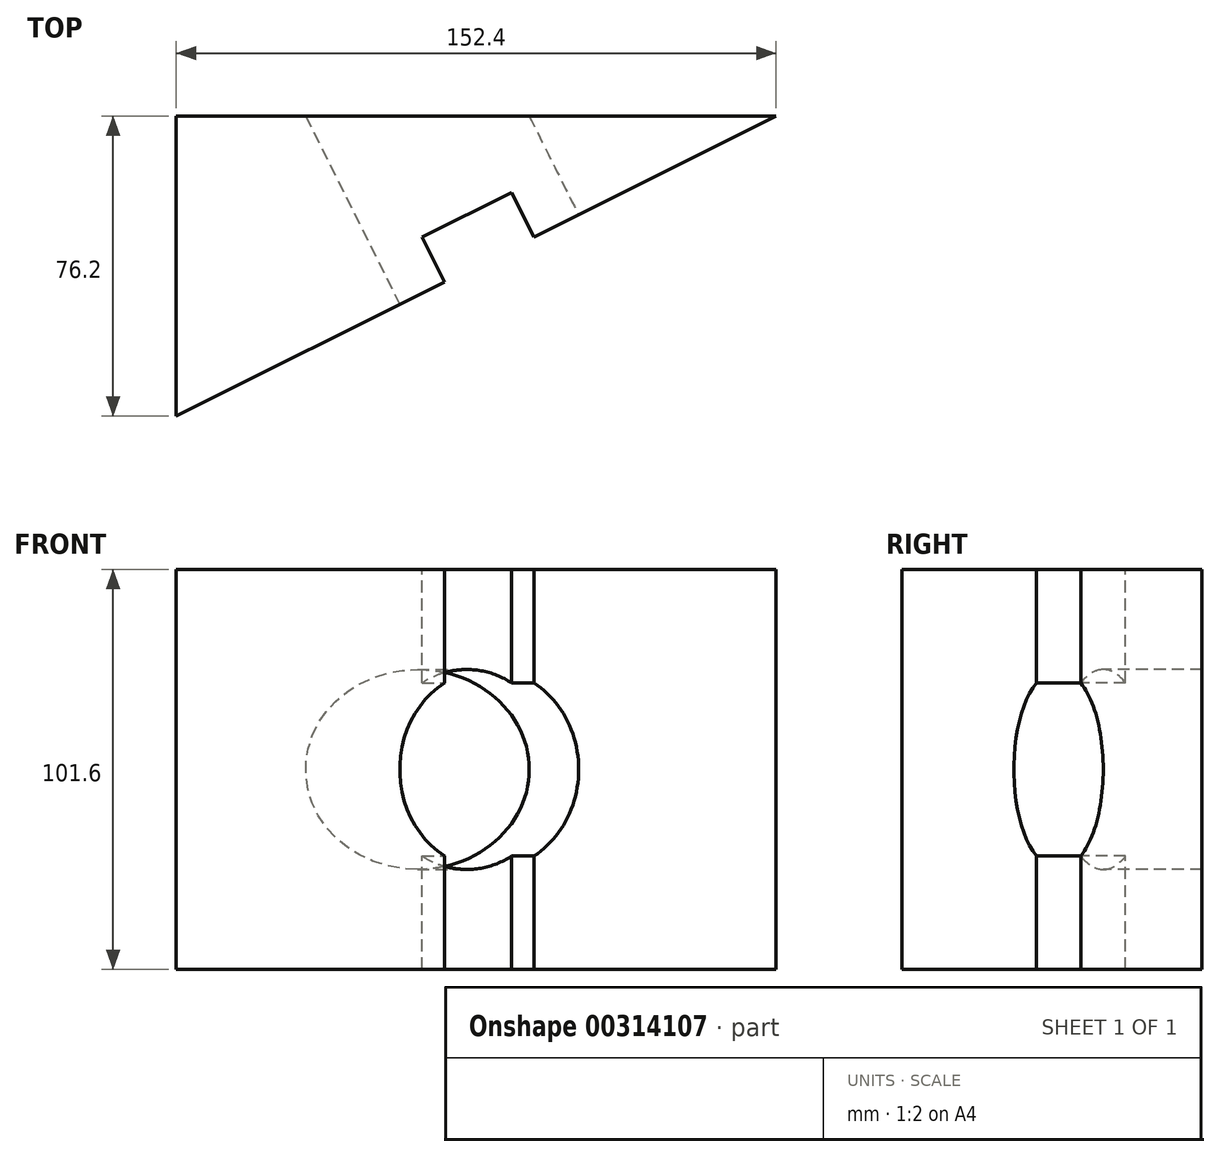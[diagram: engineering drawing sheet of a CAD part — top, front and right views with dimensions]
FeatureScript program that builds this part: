
annotation { "Feature Type Name" : "Feature", "Feature Type Description" : "" }
export const myFeature = defineFeature(function(context is Context, id is Id, definition is map)
    precondition{}
    {
        {
            var Q0;
            Q0=qCreatedBy(makeId("Top.planeOp"),FACE);
            var sketch = newSketch(context, id + "F0", { "sketchPlane" : qUnion([Q0])});
            skLineSegment(sketch, "E0.bottom", {"start": v(0, 0) * mm, "end": v(152.4, 0) * mm});
            skLineSegment(sketch, "E0.top", {"start": v(0, -76.2) * mm, "end": v(152.4, -76.2) * mm});
            skLineSegment(sketch, "E0.left", {"start": v(0, 0) * mm, "end": v(0, -76.2) * mm});
            skLineSegment(sketch, "E0.right", {"start": v(152.4, 0) * mm, "end": v(152.4, -76.2) * mm});
            skLineSegment(sketch, "E1", {"start": v(0, -76.2) * mm, "end": v(152.4, 0) * mm});
            skSolve(sketch);
        }
        {
            var Q0;
            Q0=makeQuery(id+"F0.imprint","IMPRINT",FACE,{"disambiguationData":[TD([[makeQuery(id+"F0.imprint","IMPRINT",EDGE,{"derivedFrom":sQuery(id+"F0.wireOp",EDGE,"E0.bottom")}),-1.0]])]});
            extrude(context, id + "F1", {"entities" : qUnion([Q0]), "depth" : 101.6 * mm});
        }
        {
            var Q0;
            Q0=makeQuery(id+"F1.opExtrude","SWEPT_FACE",FACE,{"disambiguationData":[OSD([sQuery(id+"F0.wireOp",EDGE,"E1")])]});
            var sketch = newSketch(context, id + "F2", { "sketchPlane" : qUnion([Q0])});
            skLineSegment(sketch, "E2.bottom", {"start": v(67.52, 0) * mm, "end": v(42.12, 0) * mm});
            skLineSegment(sketch, "E2.top", {"start": v(67.52, 101.6) * mm, "end": v(42.12, 101.6) * mm});
            skLineSegment(sketch, "E2.left", {"start": v(67.52, 0) * mm, "end": v(67.52, 101.6) * mm});
            skLineSegment(sketch, "E2.right", {"start": v(42.12, 0) * mm, "end": v(42.12, 101.6) * mm});
            skPoint(sketch, "E2.middle", {"position": v(54.82, 50.8) * mm});
            skSolve(sketch);
        }
        {
            var Q0;
            Q0 = qSketchRegion(id + "F2", true);
            extrude(context, id + "F3", {"entities" : qUnion([Q0]), "operationType" : NewBodyOperationType.REMOVE, "oppositeDirection" : true, "depth" : 12.7 * mm});
        }
        {
            var Q0;
            {var subQ0=sQuery(id+"F0.wireOp",EDGE,"E0.bottom");var subQ1=sQuery(id+"F0.wireOp",EDGE,"E1");Q0=makeQuery(id+"F3.boolean.opBoolean","SPLIT",FACE,{"disambiguationData":[TD([makeQuery(id+"F1.opExtrude","SWEPT_FACE",FACE,{"disambiguationData":[OSD([subQ0])]})])],"derivedFrom":makeQuery(id+"F1.opExtrude","SWEPT_FACE",FACE,{"disambiguationData":[OSD([subQ1])]})});}
            var sketch = newSketch(context, id + "F4", { "sketchPlane" : qUnion([Q0])});
            skCircle(sketch, "E3", {"center": v(54.82, 50.8) * mm, "radius": 25.4 * mm});
            skSolve(sketch);
        }
        {
            var Q0;
            {var subQ0=sQuery(id+"F4.wireOp",EDGE,"E3");var subQ1=makeQuery(id+"F3.boolean.opBoolean","COPY",EDGE,{"derivedFrom":makeQuery(id+"F3.opExtrude","CAP_EDGE",EDGE,{"disambiguationData":[OSD([sQuery(id+"F2.wireOp",EDGE,"E2.left")])],"isStart":true})});var subQ2=makeQuery(id+"F4.imprint","INTERSECT",VERTEX,{"disambiguationData":[OD(0.0)],"derivedFrom":[subQ1,subQ0]});Q0=makeQuery(id+"F4.imprint","IMPRINT",FACE,{"disambiguationData":[TD([[makeQuery(id+"F4.imprint","IMPRINT",EDGE,{"disambiguationData":[TD([[subQ2,1.0]])],"derivedFrom":subQ0}),1.0]])]});}
            var Q1;
            {var subQ0=sQuery(id+"F4.wireOp",EDGE,"E3");var subQ1=makeQuery(id+"F3.boolean.opBoolean","COPY",EDGE,{"derivedFrom":makeQuery(id+"F3.opExtrude","CAP_EDGE",EDGE,{"disambiguationData":[OSD([sQuery(id+"F2.wireOp",EDGE,"E2.left")])],"isStart":true})});var subQ2=makeQuery(id+"F4.imprint","INTERSECT",VERTEX,{"disambiguationData":[OD(0.0)],"derivedFrom":[subQ1,subQ0]});Q1=makeQuery(id+"F4.imprint","IMPRINT",FACE,{"disambiguationData":[TD([[makeQuery(id+"F4.imprint","IMPRINT",EDGE,{"disambiguationData":[TD([[subQ2,-1.0]])],"derivedFrom":subQ0}),1.0]])]});}
            extrude(context, id + "F5", {"entities" : qUnion([Q0, Q1]), "operationType" : NewBodyOperationType.REMOVE, "endBound" : BoundingType.THROUGH_ALL, "oppositeDirection" : true, "depth" : 25.4 * mm});
        }
    });
